# Revit family: ЭВАН В1 6-30 кВт
name_source: partatom
category: Оборудование
units: mm (PartAtom-declared; Revit-internal decimal feet)

## family parameters
Всегда вертикально = Да
Классификация = Нет
На основе рабочей плоскости = Да
Общий = Нет
При загрузке вырезать с полостями = Нет
Размер круглого соединителя = Использовать диаметр
Тип детали = Нормальный
Точка расчета площади = Нет

## types (9) — shared parameters
ADSK_Классификация нагрузок = Прочее
ADSK_Материал = Сталь
ADSK_Размер_Высота = 645 мм
ADSK_Размер_Длина = 200 мм
ADSK_Размер_Ширина = 180 мм
Dn = 16 мм
URL Ссылка = https://www.evan.ru
База = ЭЛЕКТРИЧЕСКИЙ ТЕПЛОГЕНЕРАТОР (КОТЕЛ)
Максимальная температура теплоносителя, оС = +75
Материал корпуса = Сталь
Минимально допустимое давление допустимое на входе в водонагреватель – Мпа = 0,02
Объем колбы котла, л = 7,5
Резьба патрубков для подключения трубопроводов теплоносителя = G 1/2
zero-valued in all types: Отметка по умолчанию

## per-type parameters (varying)
| type | ADSK_Количество фаз | ADSK_Номинальная мощность | ADSK_Расход теплоносителя | Потребляемая электрическая мощность при максимальной тепловой мощность  в час, кВт/ч |
| ЭВАН В1 6 кВт | 1 | 6000 Вт | 0.1 м³/ч | 6.3 |
| ЭВАН В1 7,5 кВт | 1 | 7500 Вт | 0.2 м³/ч | 7.87 |
| ЭВАН В1 21 кВт | 3 | 21000 Вт | 0.5 м³/ч | 22.02 |
| ЭВАН В1 18 кВт | 1 | 18000 Вт | 0.5 м³/ч | 18.9 |
| ЭВАН В1 30 кВт | 3 | 30000 Вт | 0.8 м³/ч | 37.8 |
| ЭВАН В1 9 кВт | 3 | 9000 Вт | 0.2 м³/ч | 9.45 |
| ЭВАН В1 12 кВт | 3 | 12000 Вт | 0.3 м³/ч | 12.6 |
| ЭВАН В1 15 кВт | 3 | 14000 Вт | 0.4 м³/ч | 15.75 |
| ЭВАН В1 24 кВт | 3 | 24000 Вт | 0.6 м³/ч | 25.2 |
